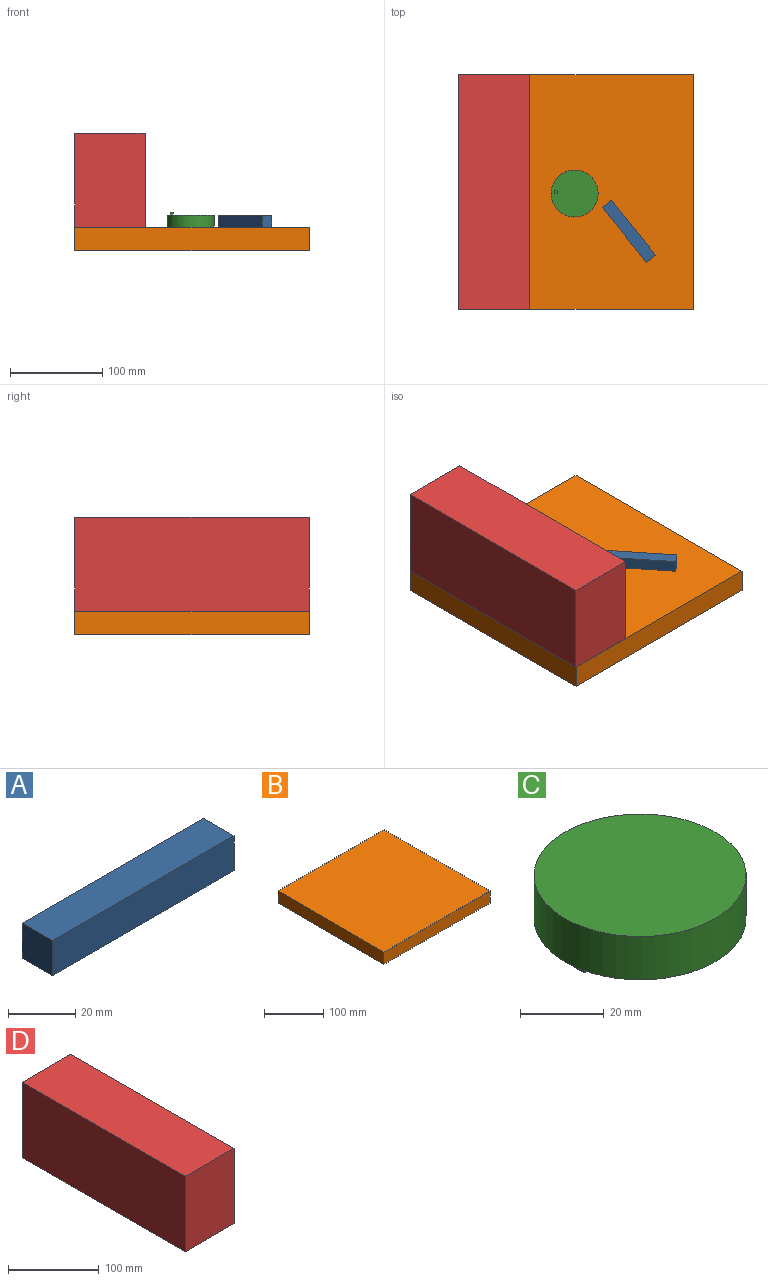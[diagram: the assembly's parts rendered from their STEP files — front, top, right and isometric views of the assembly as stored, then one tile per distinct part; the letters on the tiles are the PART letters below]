
ASSEMBLY  parts=4 mates=3
PART A: 6 faces, bbox 76.2x12.7x12.7 mm
  f0: plane 76.2x12.7mm, normal (0,0,1), area 967.7mm2, adj f1,f3,f4,f5
  f1: plane 12.7x12.7mm, normal (-1,0,0), area 161.3mm2, adj f0,f2,f4,f5
  f2: plane 76.2x12.7mm, normal (0,0,-1), area 967.7mm2, adj f1,f3,f4,f5
  f3: plane 12.7x12.7mm, normal (1,0,0), area 161.3mm2, adj f0,f2,f4,f5
  f4: plane 76.2x12.7mm, normal (0,-1,0), area 967.7mm2, adj f0,f1,f2,f3
  f5: plane 76.2x12.7mm, normal (0,1,0), area 967.7mm2, adj f0,f1,f2,f3
PART B: 6 faces, bbox 254x254x25.4 mm
  f0: plane 254x25.4mm, normal (1,0,0), area 6451.6mm2, adj f1,f3,f4,f5
  f1: plane 254x25.4mm, normal (0,1,0), area 6451.6mm2, adj f0,f2,f4,f5
  f2: plane 254x25.4mm, normal (-1,0,0), area 6451.6mm2, adj f1,f3,f4,f5
  f3: plane 254x25.4mm, normal (0,-1,0), area 6451.6mm2, adj f0,f2,f4,f5
  f4: plane 254x254mm, normal (0,0,1), area 64516mm2, adj f0,f1,f2,f3
  f5: plane 254x254mm, normal (0,0,-1), area 64516mm2, adj f0,f1,f2,f3
PART C: 8 faces, bbox 50.8x50.8x15.9 mm
  f0: cylinder r=25.4mm len=50.8mm, axis (0,0,1), area 2026.8mm2, adj f1,f2
  f1: plane 50.8x50.8mm, normal (0,0,-1), area 2016.7mm2, adj f0,f3,f4,f5,f6
  f2: plane 50.8x50.8mm, normal (0,0,1), area 2026.8mm2, adj f0
  f3: plane 3.18x3.1mm, normal (0,1,0), area 9.8mm2, adj f1,f4,f6,f7
  f4: plane 3.26x3.18mm, normal (1,0,0), area 10.3mm2, adj f1,f3,f5,f7
  f5: plane 3.18x3.1mm, normal (0,-1,0), area 9.8mm2, adj f1,f4,f6,f7
  f6: plane 3.26x3.18mm, normal (-1,0,0), area 10.3mm2, adj f1,f3,f5,f7
  f7: plane 3.26x3.1mm, normal (0,0,-1), area 10.1mm2, adj f3,f4,f5,f6
PART D: 10 faces, bbox 76.2x254x101.6 mm
  f0: plane 254x76.2mm, normal (0,0,-1), area 6315.6mm2, adj f1,f3,f4,f5,f6,f7,f9
  f1: plane 254x101.6mm, normal (1,0,0), area 9411.3mm2, adj f0,f2,f4,f5,f6,f7,f8
  f2: plane 254x76.2mm, normal (0,0,1), area 19354.8mm2, adj f1,f3,f4,f5
  f3: plane 254x101.6mm, normal (-1,0,0), area 25806.4mm2, adj f0,f2,f4,f5
  f4: plane 101.6x76.2mm, normal (0,-1,0), area 7741.9mm2, adj f0,f1,f2,f3
  f5: plane 101.6x76.2mm, normal (0,1,0), area 7741.9mm2, adj f0,f1,f2,f3
  f6: plane 79.84x63.5mm, normal (0,1,0), area 5070mm2, adj f0,f1,f8,f9
  f7: plane 79.84x63.5mm, normal (0,-1,0), area 5070mm2, adj f0,f1,f8,f9
  f8: plane 205.34x63.5mm, normal (0,0,-1), area 13039.2mm2, adj f1,f6,f7,f9
  f9: plane 205.34x79.84mm, normal (1,0,0), area 16395.1mm2, adj f0,f6,f7,f8
PLACE A rot(axis=(0,0,1),128.7deg) t=(100.89,-107.04,72.35)mm
PLACE B at identity fixed
PLACE C rot(axis=(1,0,0),180deg) t=(-94.16,61.07,25.59)mm
PLACE D t=(-36.15,127,-19.19)mm
MATE fastened B.f4 <-> D.f0  axis (0,0,1) through (-127,0,25.4)mm
MATE slider C.f6 <-> D.f9  axis (-1,0,0) through (-23.62,0,39.88)mm
MATE revolute A.f2 <-> B.f4  axis (0,0,-1) through (76.2,-76.2,25.4)mm
